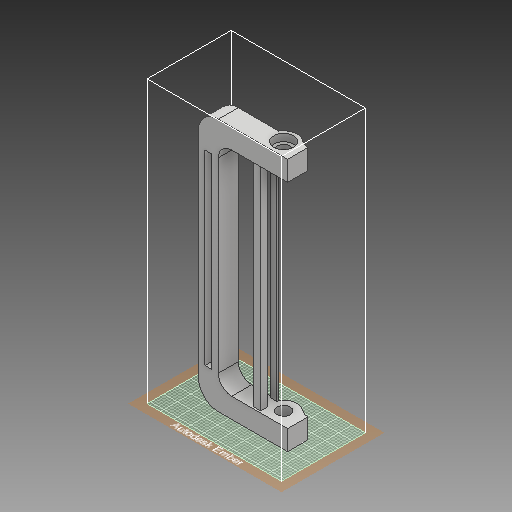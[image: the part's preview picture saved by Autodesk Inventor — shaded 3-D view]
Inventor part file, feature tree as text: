
AUTODESK INVENTOR PART (.ipt)
format: ipt  version: 2018 (Build 220112000, 112)  size: 519,680 bytes
history: native  units: in
note: dims shown in document units (in); Inventor stores cm internally (conversion verified against a paired STEP export)
features: sketch x36, extrude x22, fillet x7, hole x2, plane x1, mirror x1
ambient origin geometry x8: Origin, YZ Plane, XZ Plane, XY Plane, X Axis, Y Axis, Z Axis, Center Point
bodies: Solid1 (feature_tree)
feature tree (69):
  extrude  "Extrusion1"  Depth=0.375in
  sketch  "Sketch2"  dims[d3=0.375in d4=0.5in d5=0.375in d6=0.0in]
  extrude  "Extrusion2"  Depth=0.375in
  fillet  "Fillet1"  Radius=0.375in
  extrude  "Extrusion3"  Depth=0.375in
  extrude  "Extrusion4"  Depth=0.25in
  plane  "Work Plane1"
  mirror  "Mirror1"
  fillet  "Fillet2"  Radius=0.24in
  extrude  "Extrusion5"  Depth=0.375in
  sketch  "Sketch6"  dims[d17=1.0in d18=0.0in d19=0.24in d20=0.0in]
  extrude  "Extrusion6"  Depth=0.24in TaperAngle=0.0deg
  extrude  "Extrusion7"  Depth=0.375in
  fillet  "Fillet3"  Radius=0.25in
  fillet  "Fillet4"  Radius=0.375in
  fillet  "Fillet5"  Radius=0.25in
  fillet  "Fillet6"  Radius=0.125in
  sketch  "Sketch9"  dims[d30=0.125in d31=0.125in]
  extrude  "Extrusion8"  Depth=0.035in
  sketch  "Sketch11"  dims[d35=0.2in]
  sketch  "Sketch12"  dims[d36=0.2in d37=0.75in d38=0.375in d39=0.25in d40=0.5635in d41=0.35in d42=0.0in]
  hole  "Hole1"  [1 undecoded]
  hole  "Hole2"  [1 undecoded]
  sketch  "Sketch14"  dims[d51=3.5in d52=0.375in d53=0.0in]
  extrude  "Extrusion9"  Depth=0.125in
  sketch  "Sketch16"  dims[d58=0.4375in d59=0.0in d60=0.0625in d61=0.0in]
  extrude  "Extrusion10"  Depth=0.375in TaperAngle=0.0deg
  extrude  "Extrusion11"  Depth=0.25in
  extrude  "Extrusion12"  Depth=0.0625in TaperAngle=0.0deg
  sketch  "Sketch20"  dims[d72=0.39in d73=0.135in d74=0.0in]
  sketch  "Sketch21"  dims[d75=0.39in d76=0.135in d77=0.0in]
  sketch  "Sketch22"  dims[d78=0.4475in d79=0.0in d80=0.375in d81=0.0in]
  extrude  "Extrusion13"  Depth=0.125in
  extrude  "Extrusion14"  Depth=0.25in TaperAngle=0.0deg
  fillet  "Fillet7"  Radius=0.25in
  extrude  "Extrusion15"  Depth=0.125in
  extrude  "Extrusion16"  Depth=0.135in TaperAngle=0.0deg
  extrude  "Extrusion17"  Depth=0.135in TaperAngle=0.0deg
  extrude  "Extrusion18"  Depth=0.375in TaperAngle=0.0deg
  sketch  "Sketch29"
  extrude  "Extrusion19"  Depth=0.375in TaperAngle=0.0deg
  sketch  "Sketch31"
  extrude  "Extrusion20"  Depth=0.375in TaperAngle=0.0deg
  extrude  "Extrusion21"  Depth=0.125in
  sketch  "Sketch34"
  sketch  "Sketch35"
  extrude  "Extrusion22"  Depth=0.375in TaperAngle=0.0deg
  sketch  "Sketch1"  dims[d0=1.3in d1=0.375in]
  sketch  "Sketch3"  dims[d7=0.375in d8=0.0in d9=0.375in]
  sketch  "Sketch4"  dims[d10=0.24in d11=0.0in d12=0.25in d13=0.24in d14=0.0in]
  sketch  "Sketch5"  dims[d15=2.0in d16=0.375in]
  sketch  "Sketch7"  dims[d21=0.375in d22=0.0in d23=0.375in d24=0.25in d25=0.375in d26=0.25in d27=0.125in]
  sketch  "Sketch8"  dims[d28=0.035in d29=0.035in]
  sketch  "Sketch10"  dims[d32=4.375in d33=0.0in d34=0.2in]
  sketch  "Sketch13"  dims[d43=0.2in d44=0.75in d45=0.375in d46=0.25in d47=0.5635in d48=0.35in d49=0.0in d50=0.125in]
  sketch  "Sketch15"  dims[d56=0.25in d57=0.25in]
  sketch  "Sketch17"  dims[d62=0.04in d63=0.0in d64=0.125in]
  sketch  "Sketch18"  dims[d65=0.075in d66=4.04in d67=0.0in d68=0.25in]
  sketch  "Sketch19"  dims[d69=0.075in d70=0.0in d71=0.125in]
  sketch  "Sketch23"  dims[d82=0.25in d83=0.375in d84=0.0in]
  sketch  "Sketch24"  dims[d85=0.125in d86=0.375in d87=0.0in]
  sketch  "Sketch25"  dims[d88=0.125in d89=0.0in d90=0.125in]
  sketch  "Sketch26"  dims[d91=0.15in d92=0.375in d93=0.0in]
  sketch  "Sketch27"
  sketch  "Sketch28"
  sketch  "Sketch30"
  sketch  "Sketch32"
  sketch  "Sketch33"
  sketch  "Sketch36"
note: 2 required parameter values undecoded (feature->parameter linkage not recoverable at this tier; creation-order binding heuristic only, values carry confidence <= 0.55)
